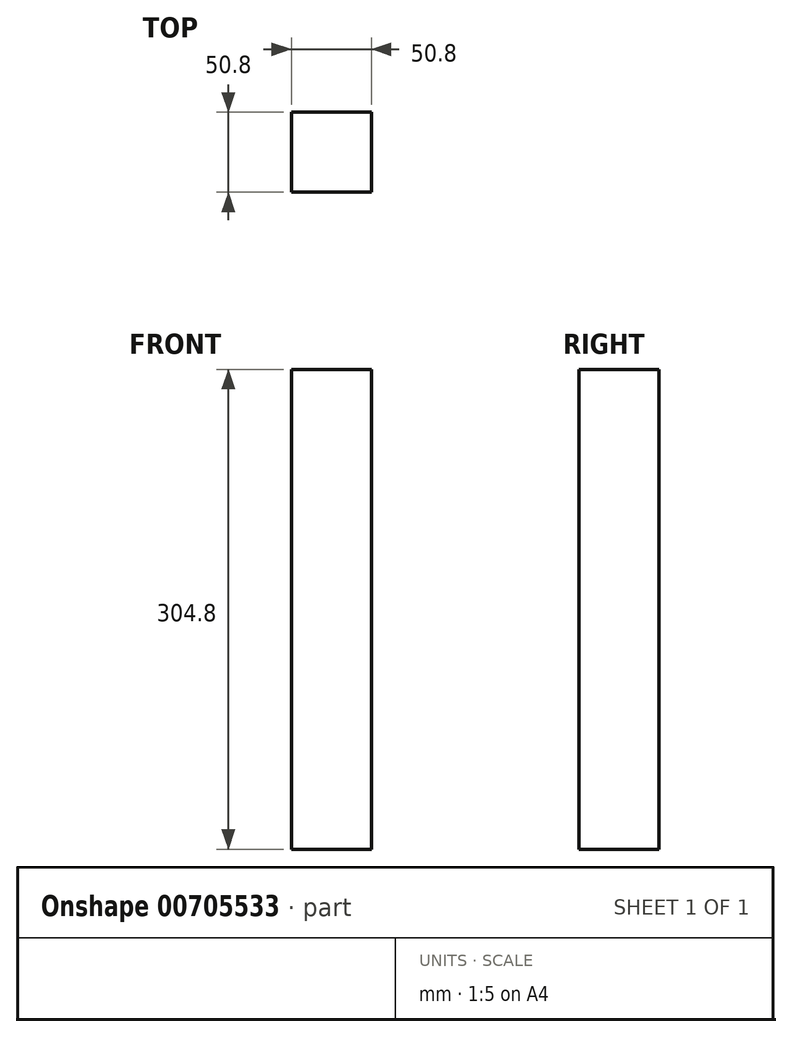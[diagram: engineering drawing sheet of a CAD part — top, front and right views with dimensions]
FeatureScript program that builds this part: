
annotation { "Feature Type Name" : "Feature", "Feature Type Description" : "" }
export const myFeature = defineFeature(function(context is Context, id is Id, definition is map)
    precondition{}
    {
        {
            var Q0;
            Q0=qCreatedBy(makeId("Top.planeOp"),FACE);
            var sketch = newSketch(context, id + "F0", { "sketchPlane" : qUnion([Q0])});
            skLineSegment(sketch, "E0.bottom", {"start": v(-33.76, 29.22) * mm, "end": v(17.04, 29.22) * mm});
            skLineSegment(sketch, "E0.top", {"start": v(-33.76, -21.58) * mm, "end": v(17.04, -21.58) * mm});
            skLineSegment(sketch, "E0.left", {"start": v(-33.76, 29.22) * mm, "end": v(-33.76, -21.58) * mm});
            skLineSegment(sketch, "E0.right", {"start": v(17.04, 29.22) * mm, "end": v(17.04, -21.58) * mm});
            skPoint(sketch, "E0.middle", {"position": v(-8.36, 3.82) * mm});
            skSolve(sketch);
        }
        {
            var Q0;
            Q0 = qSketchRegion(id + "F0", true);
            extrude(context, id + "F1", {"entities" : qUnion([Q0]), "depth" : 304.8 * mm, "offsetDistance" : 25.4 * mm});
        }
    });
